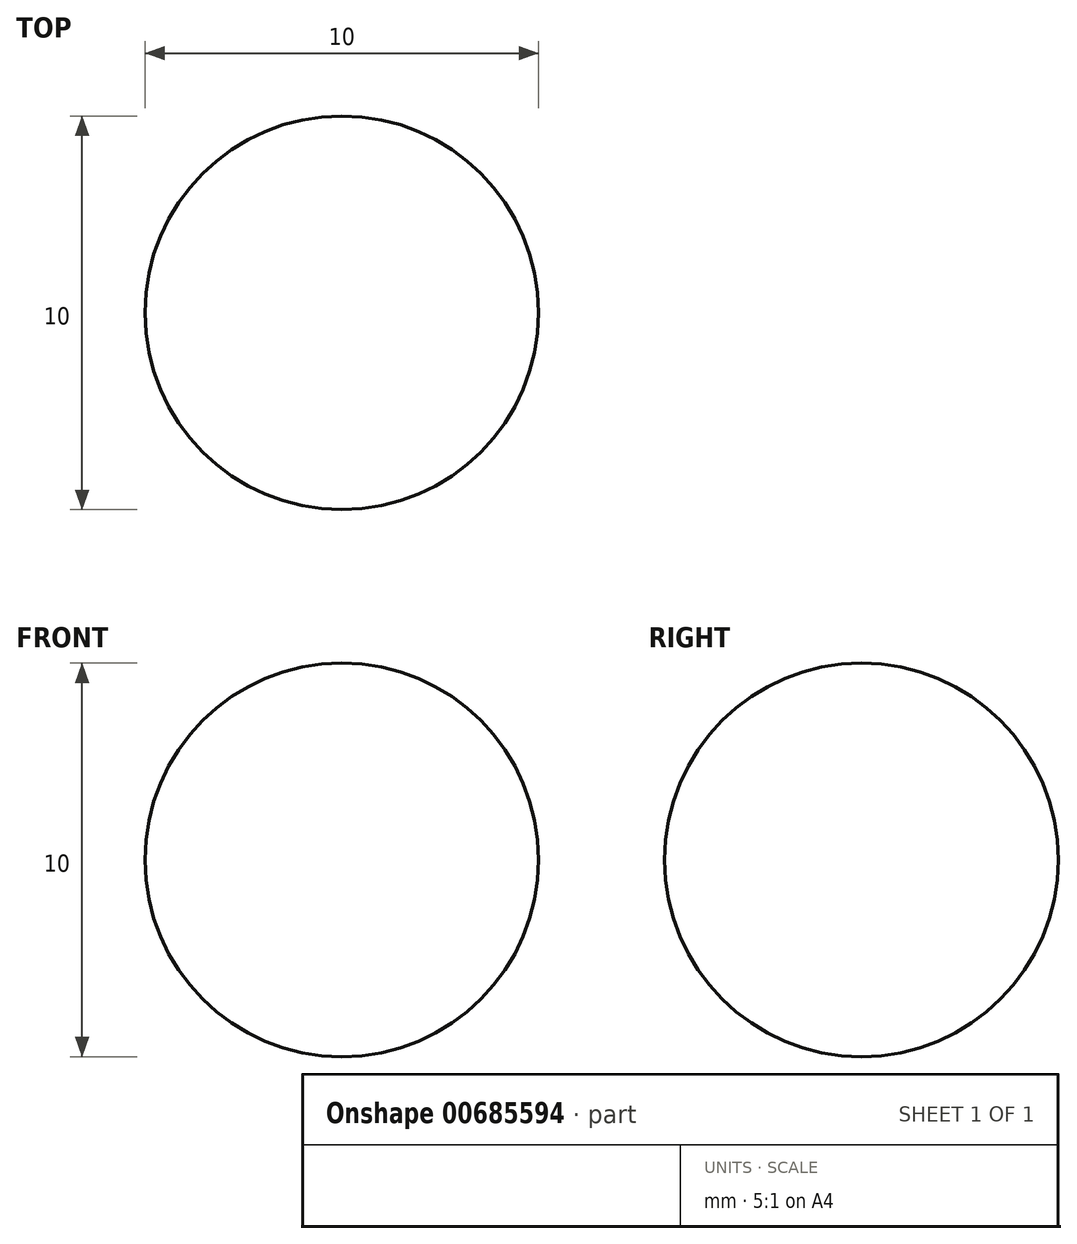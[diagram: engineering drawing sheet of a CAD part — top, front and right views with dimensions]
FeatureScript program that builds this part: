
annotation { "Feature Type Name" : "Feature", "Feature Type Description" : "" }
export const myFeature = defineFeature(function(context is Context, id is Id, definition is map)
    precondition{}
    {
        {
            var Q0;
            Q0=qCreatedBy(makeId("Front.planeOp"),FACE);
            var sketch = newSketch(context, id + "F0", { "sketchPlane" : qUnion([Q0])});
            skArc(sketch, "E0", {"start": v(0, -5) * mm, "mid": v(5, 0) * mm, "end": v(0, 5) * mm});
            skLineSegment(sketch, "E1", {"start": v(0, 5) * mm, "end": v(0, -5) * mm});
            skSolve(sketch);
        }
        {
            var Q0;
            Q0=makeQuery(id+"F0.imprint","IMPRINT",FACE,{"disambiguationData":[TD([[makeQuery(id+"F0.imprint","IMPRINT",EDGE,{"derivedFrom":sQuery(id+"F0.wireOp",EDGE,"E0")}),1.0]])]});
            var Q1;
            Q1=sQuery(id+"F0.wireOp",EDGE,"E1");
            revolve(context, id + "F1", {"entities" : qUnion([Q0]), "axis" : qUnion([Q1]), "revolveType" : RevolveType.FULL});
        }
    });
